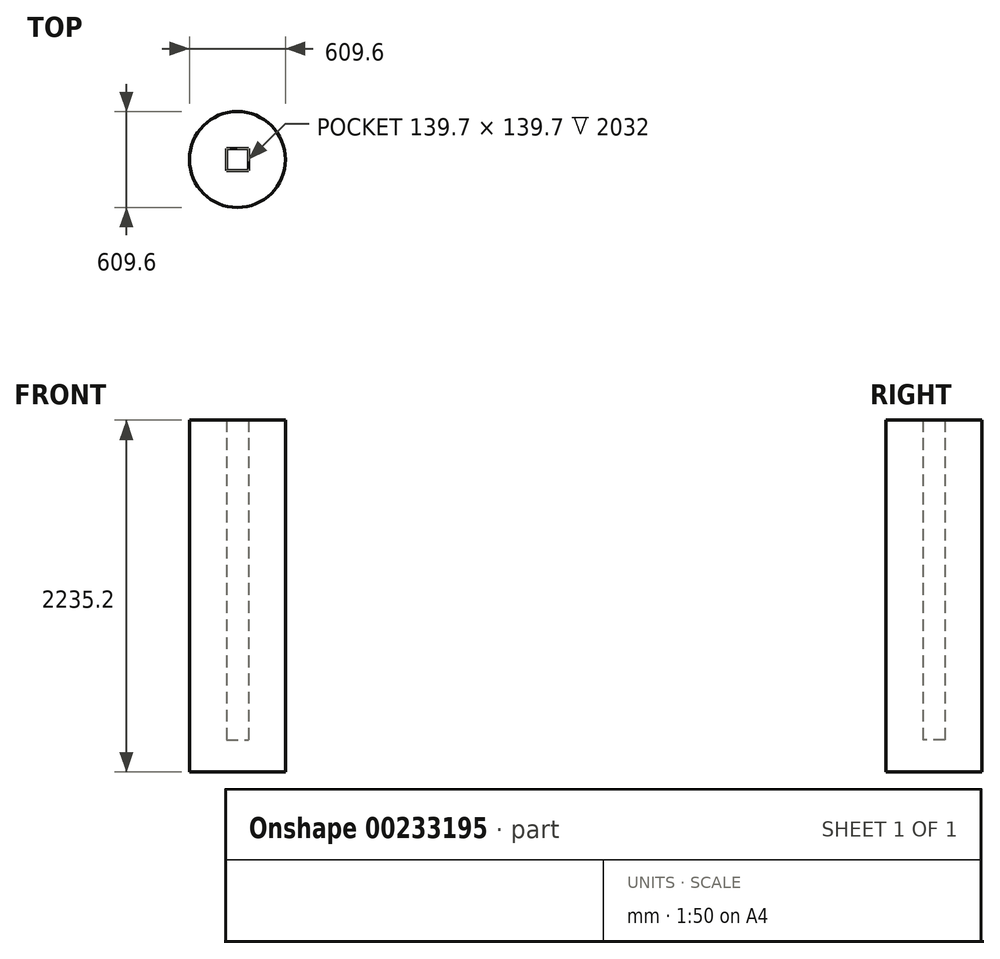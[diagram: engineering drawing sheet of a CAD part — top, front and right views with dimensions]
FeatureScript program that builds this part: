
annotation { "Feature Type Name" : "Feature", "Feature Type Description" : "" }
export const myFeature = defineFeature(function(context is Context, id is Id, definition is map)
    precondition{}
    {
        {
            var Q0;
            Q0=qCreatedBy(makeId("Top.planeOp"),FACE);
            var sketch = newSketch(context, id + "F0", { "sketchPlane" : qUnion([Q0])});
            skCircle(sketch, "E0", {"center": v(-19.36, -13.43) * mm, "radius": 304.8 * mm});
            skLineSegment(sketch, "E1.bottom", {"start": v(-89.2, 56.42) * mm, "end": v(50.5, 56.42) * mm});
            skLineSegment(sketch, "E1.top", {"start": v(-89.2, -83.28) * mm, "end": v(50.5, -83.28) * mm});
            skLineSegment(sketch, "E1.left", {"start": v(-89.2, 56.42) * mm, "end": v(-89.2, -83.28) * mm});
            skLineSegment(sketch, "E1.right", {"start": v(50.5, 56.42) * mm, "end": v(50.5, -83.28) * mm});
            skSolve(sketch);
        }
        {
            var Q0;
            Q0 = qSketchRegion(id + "F0", true);
            extrude(context, id + "F1", {"entities" : qUnion([Q0]), "depth" : 2235.2 * mm});
        }
        {
            var Q0;
            Q0=makeQuery(id+"F0.imprint","IMPRINT",FACE,{"disambiguationData":[TD([[makeQuery(id+"F0.imprint","IMPRINT",EDGE,{"derivedFrom":sQuery(id+"F0.wireOp",EDGE,"E1.bottom")}),-1.0]])]});
            extrude(context, id + "F2", {"entities" : qUnion([Q0]), "operationType" : NewBodyOperationType.ADD, "depth" : 203.2 * mm});
        }
    });
